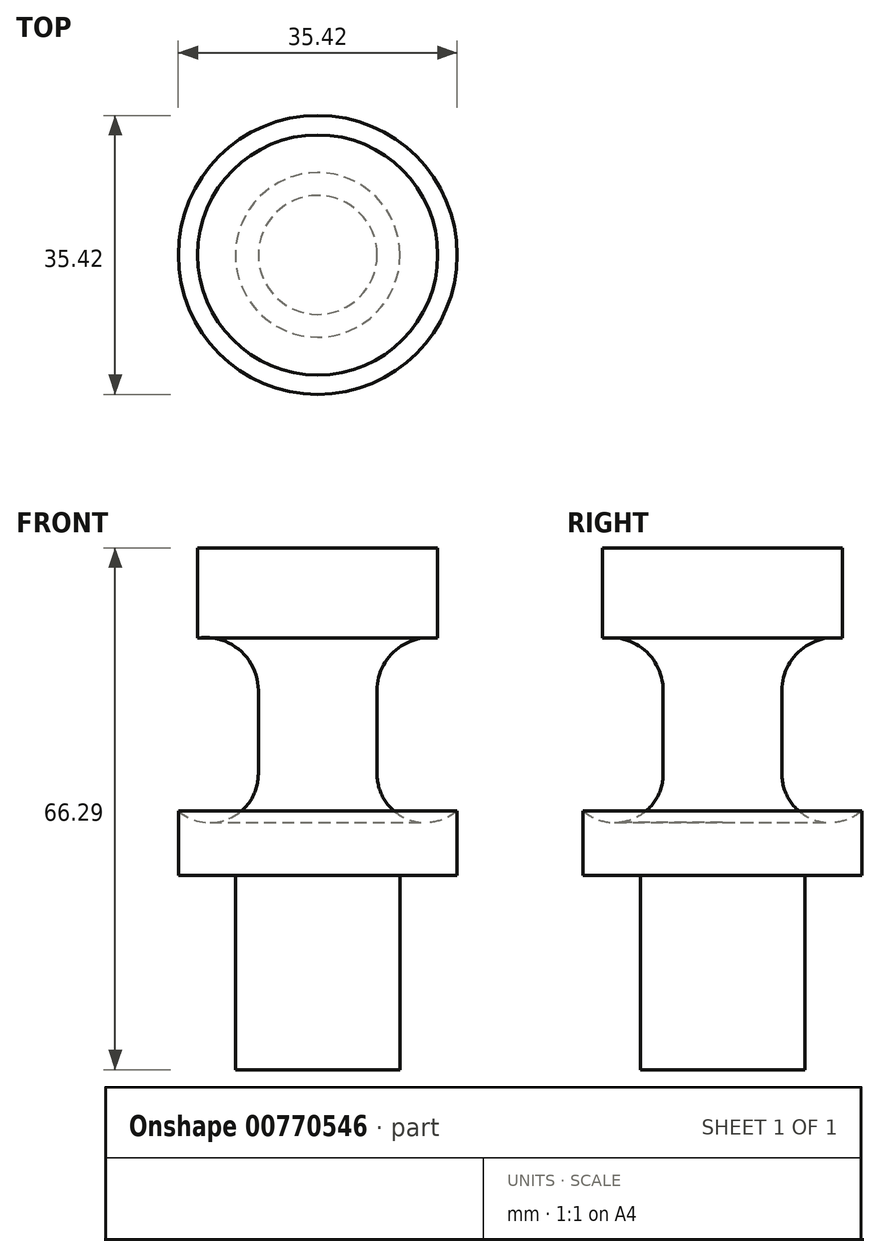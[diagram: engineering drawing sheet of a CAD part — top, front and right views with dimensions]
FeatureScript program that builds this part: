
annotation { "Feature Type Name" : "Feature", "Feature Type Description" : "" }
export const myFeature = defineFeature(function(context is Context, id is Id, definition is map)
    precondition{}
    {
        {
            var Q0;
            Q0=qCreatedBy(makeId("Front.planeOp"),FACE);
            var sketch = newSketch(context, id + "F0", { "sketchPlane" : qUnion([Q0])});
            skLineSegment(sketch, "E0", {"start": v(0, 0) * mm, "end": v(0, 41.61) * mm});
            skLineSegment(sketch, "E1", {"start": v(0, 41.61) * mm, "end": v(0, 41.61) * mm});
            skLineSegment(sketch, "E2", {"start": v(0, 41.61) * mm, "end": v(15.25, 41.61) * mm});
            skLineSegment(sketch, "E3", {"start": v(15.25, 41.61) * mm, "end": v(15.25, 30.16) * mm});
            skLineSegment(sketch, "E4", {"start": v(7.54, 23.49) * mm, "end": v(7.54, 12.86) * mm});
            skLineSegment(sketch, "E5", {"start": v(10.45, 0) * mm, "end": v(17.7, 0) * mm});
            skLineSegment(sketch, "E6", {"start": v(17.7, 0) * mm, "end": v(17.7, 8.2) * mm});
            skArc(sketch, "E7", {"start": v(15.25, 30.16) * mm, "mid": v(9.87, 28.58) * mm, "end": v(7.54, 23.49) * mm});
            skArc(sketch, "E8", {"start": v(7.54, 12.86) * mm, "mid": v(11.13, 7.27) * mm, "end": v(17.7, 8.2) * mm});
            skLineSegment(sketch, "E9", {"start": v(0, 0) * mm, "end": v(0, -24.68) * mm});
            skLineSegment(sketch, "E10", {"start": v(0, -24.68) * mm, "end": v(10.45, -24.68) * mm});
            skLineSegment(sketch, "E11", {"start": v(10.45, -24.68) * mm, "end": v(10.45, 0) * mm});
            skSolve(sketch);
        }
        {
            var Q0;
            Q0=makeQuery(id+"F0.imprint","IMPRINT",FACE,{"disambiguationData":[TD([[makeQuery(id+"F0.imprint","IMPRINT",EDGE,{"derivedFrom":sQuery(id+"F0.wireOp",EDGE,"E0")}),-1.0]])]});
            var Q1;
            Q1=sQuery(id+"F0.wireOp",EDGE,"E0");
            revolve(context, id + "F1", {"surfaceOperationType" : NewSurfaceOperationType.NEW, "entities" : qUnion([Q0]), "axis" : qUnion([Q1]), "revolveType" : RevolveType.FULL});
        }
    });
